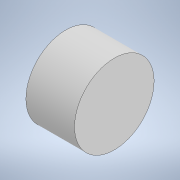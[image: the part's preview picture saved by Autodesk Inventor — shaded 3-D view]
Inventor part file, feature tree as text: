
AUTODESK INVENTOR PART (.ipt)
format: ipt  version: 2020 (Build 240168000, 168)  size: 109,568 bytes
history: native  units: in
note: dims shown in document units (in); Inventor stores cm internally (conversion verified against a paired STEP export)
features: extrude x2, sketch x2
ambient origin geometry x8: Origin, YZ Plane, XZ Plane, XY Plane, X Axis, Y Axis, Z Axis, Center Point
bodies: Solid1 (feature_tree)
feature tree (4):
  extrude  "Extrusion1"  Depth=0.1575in
  extrude  "Extrusion2"  Depth=0.2756in
  sketch  "Sketch1"  dims[d0=0.7087in d1=0.1575in]
  sketch  "Sketch2"  dims[d2=0.0in d4=0.2756in d5=0.0in]
